# Revit family: ROSENBERG_RS
name_source: partatom
category: Wyposażenie mechaniczne
revit_build: Autodesk Revit 2017 (Build: 20160225_1515(x64)
units: mm (PartAtom-declared; Revit-internal decimal feet)

## family parameters
Numer OmniClass = 23.75.00.00
Oparty na płaszczyźnie roboczej = Nie
Punkt obliczania pomieszczeń = Nie
Tnij formami wycięć po wczytaniu = Nie
Typ części = Dzieli na
Tytuł OmniClass = Climate Control (HVAC)
Współdzielony = Tak
Wymiar okrągłego złącza = Użyj średnicy
Zawsze pionowo = Tak

## types (10) — shared parameters
Date = 10.2018
Frequency = 50 Hz
Materiał = <Wg kategorii>
Opis = Wentylator kanałowy
Producent = Rosenberg
Protection_Class = IP44
URL = https://www.rosenberg.pl
Version = 1
Voltage = 230 V
param._Puszka wysokość = 120 mm  [stored 0.393701 ft]
param_Wysokość kołnierza = 30 mm  [stored 0.0984252 ft]

## per-type parameters (varying)
| type | Air_flow | Current | Diameter_connection | Power | Pressure | Weight | param_Długość wentylatora | param_Puszka długość | param_Puszka odsunięcie | param_Puszka szerokość | param_Sr.wenty | param_Szerokość wentylatora | param_b1 | param_f1 | param_wymiar ramienia |
| 100 L.2CA | 0.0 m³/h | 0 A | 100 mm  [stored 0.328084 ft] | 29 W | 0.0 Pa | 2.00 kg | 220 mm | 120 mm  [stored 0.393701 ft] | 60 mm | 62 mm  [stored 0.203412 ft] | 95 mm | 245 mm  [stored 0.803806 ft] | 55 mm | 147 mm | 245 mm  [stored 0.803806 ft] |
| 150.3CA | 311.0 m³/h | 0 A | 149 mm | 52 W | 188.0 Pa | 3.00 kg | 241 mm | 140 mm | 80 mm | 90 mm | 144 mm | 341 mm | 60 mm | 161 mm | 341 mm |
| 160.3CA | 261.0 m³/h | 0 A | 159 mm | 49 W | 200.0 Pa | 3.00 kg | 241 mm | 140 mm | 80 mm | 90 mm | 154 mm | 341 mm | 60 mm | 161 mm | 341 mm |
| 160 L.3CF | 409.0 m³/h | 0 A | 159 mm | 101 W | 256.0 Pa | 3.50 kg | 239 mm | 140 mm | 80 mm | 90 mm | 154 mm | 341 mm | 60 mm | 159 mm | 341 mm |
| 250 L.3DF | 567.0 m³/h | 1 A | 249 mm | 130 W | 292.0 Pa | 4.60 kg | 247 mm | 140 mm | 100 mm  [stored 0.328084 ft] | 70 mm  [stored 0.229659 ft] | 244 mm | 341 mm | 62 mm  [stored 0.203412 ft] | 165 mm | 341 mm |
| 200.3CF | 431.0 m³/h | 0 A | 199 mm | 102 W | 259.0 Pa | 3.80 kg | 242 mm | 140 mm | 100 mm  [stored 0.328084 ft] | 70 mm  [stored 0.229659 ft] | 194 mm | 341 mm | 61 mm | 161 mm | 341 mm |
| 315.3EF | 622.0 m³/h | 1 A | 314 mm | 170 W | 368.0 Pa | 5.70 kg | 275 mm | 180 mm  [stored 0.590551 ft] | 132 mm  [stored 0.433071 ft] | 70 mm  [stored 0.229659 ft] | 309 mm  [stored 1.01378 ft] | 405 mm | 69 mm | 183 mm | 405 mm |
| 315 M.3EF | 622.0 m³/h | 1 A | 314 mm | 200 W | 387.0 Pa | 5.80 kg | 275 mm | 180 mm  [stored 0.590551 ft] | 132 mm  [stored 0.433071 ft] | 70 mm  [stored 0.229659 ft] | 309 mm  [stored 1.01378 ft] | 405 mm | 69 mm | 183 mm | 405 mm |
| 125 L.3CA | 175.0 m³/h | 0 A | 124 mm  [stored 0.406824 ft] | 42 W | 213.0 Pa | 2.50 kg | 221 mm  [stored 0.725066 ft] | 120 mm  [stored 0.393701 ft] | 60 mm | 62 mm  [stored 0.203412 ft] | 119 mm  [stored 0.39042 ft] | 245 mm  [stored 0.803806 ft] | 55 mm | 147 mm | 245 mm  [stored 0.803806 ft] |
| 250.3CF | 477.0 m³/h | 0 A | 249 mm | 104 W | 237.0 Pa | 3.70 kg | 243 mm | 140 mm | 100 mm  [stored 0.328084 ft] | 70 mm  [stored 0.229659 ft] | 244 mm | 341 mm | 61 mm | 162 mm | 341 mm |

note: column(s) folded — value = type name in every type: Model

note: [stored X ft] marks values corroborated as IEEE doubles in the binary element streams (Revit-internal decimal feet)

## geometry (parser evidence)
native form markers: Blend x4, Sweep x4
no freeform markers — native parametric forms only
